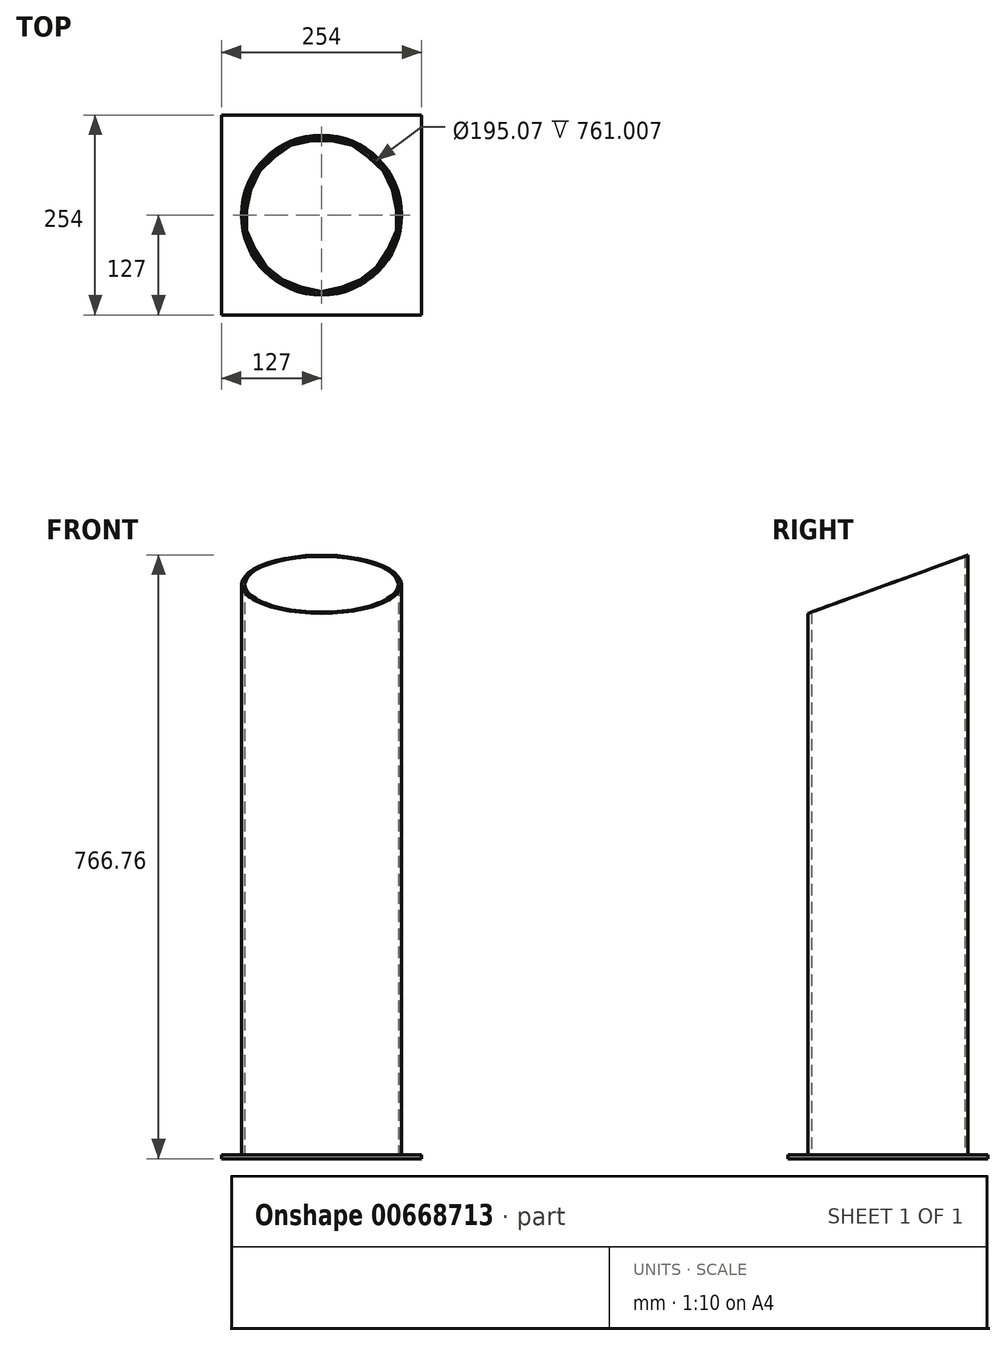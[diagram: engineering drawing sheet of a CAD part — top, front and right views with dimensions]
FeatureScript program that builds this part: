
annotation { "Feature Type Name" : "Feature", "Feature Type Description" : "" }
export const myFeature = defineFeature(function(context is Context, id is Id, definition is map)
    precondition{}
    {
        {
            var Q0;
            Q0=qCreatedBy(makeId("Top.planeOp"),FACE);
            var sketch = newSketch(context, id + "F0", { "sketchPlane" : qUnion([Q0])});
            skCircle(sketch, "E0", {"center": v(0, 0) * mm, "radius": 101.6 * mm});
            skCircle(sketch, "E1.0", {"center": v(0, 0) * mm, "radius": 97.54 * mm});
            skSolve(sketch);
        }
        {
            var Q0;
            Q0=qSketchRegion(id+"F0",true);
            extrude(context, id + "F1", {"entities" : qUnion([Q0]), "depth" : 762 * mm});
        }
        {
            var Q0;
            Q0=qCreatedBy(makeId("Top.planeOp"),FACE);
            var sketch = newSketch(context, id + "F2", { "sketchPlane" : qUnion([Q0])});
            skLineSegment(sketch, "E2.bottom", {"start": v(127, 127) * mm, "end": v(-127, 127) * mm});
            skLineSegment(sketch, "E2.top", {"start": v(127, -127) * mm, "end": v(-127, -127) * mm});
            skLineSegment(sketch, "E2.left", {"start": v(127, 127) * mm, "end": v(127, -127) * mm});
            skLineSegment(sketch, "E2.right", {"start": v(-127, 127) * mm, "end": v(-127, -127) * mm});
            skPoint(sketch, "E2.middle", {"position": v(0, 0) * mm});
            skSolve(sketch);
        }
        {
            var Q0;
            Q0=qSketchRegion(id+"F2",true);
            extrude(context, id + "F3", {"entities" : qUnion([Q0]), "operationType" : NewBodyOperationType.ADD, "oppositeDirection" : true, "depth" : 4.76 * mm});
        }
        {
            var Q0;
            Q0=qCreatedBy(makeId("Right.planeOp"),FACE);
            var sketch = newSketch(context, id + "F4", { "sketchPlane" : qUnion([Q0])});
            skPoint(sketch, "E3.middle", {"position": v(0, 441.03) * mm});
            skPoint(sketch, "E3.top.start.orphan", {"position": v(-208.83, 272.47) * mm});
            skPoint(sketch, "E3.right.start.orphan", {"position": v(208.83, 609.6) * mm});
            skPoint(sketch, "E4.orphan", {"position": v(412.03, 609.6) * mm});
            skPoint(sketch, "E5.start.orphan", {"position": v(-412.03, 272.47) * mm});
            skLineSegment(sketch, "E6.bottom", {"start": v(101.6, 762) * mm, "end": v(-101.6, 762) * mm});
            skLineSegment(sketch, "E6.right", {"start": v(-101.6, 762) * mm, "end": v(-101.6, 688.04) * mm});
            skPoint(sketch, "E6.middle", {"position": v(0, 725.02) * mm});
            skLineSegment(sketch, "E7", {"start": v(-101.6, 688.04) * mm, "end": v(101.6, 762) * mm});
            skPoint(sketch, "E6.top.start.orphan", {"position": v(101.6, 688.04) * mm});
            skSolve(sketch);
        }
        {
            var Q0;
            Q0=qSketchRegion(id+"F4",true);
            extrude(context, id + "F5", {"entities" : qUnion([Q0]), "operationType" : NewBodyOperationType.REMOVE, "endBound" : BoundingType.THROUGH_ALL, "oppositeDirection" : true, "depth" : 25.4 * mm, "hasSecondDirection" : true, "secondDirectionBound" : SecondDirectionBoundingType.THROUGH_ALL, "secondDirectionOppositeDirection" : false, "secondDirectionDepth" : 25.4 * mm});
        }
        {
            var Q0;
            Q0=qSketchRegion(id+"F4",true);
            extrude(context, id + "F6", {"entities" : qUnion([Q0]), "operationType" : NewBodyOperationType.REMOVE, "endBound" : BoundingType.THROUGH_ALL, "depth" : 25.4 * mm, "hasSecondDirection" : true, "secondDirectionBound" : SecondDirectionBoundingType.THROUGH_ALL, "secondDirectionOppositeDirection" : true, "secondDirectionDepth" : 25.4 * mm});
        }
    });
